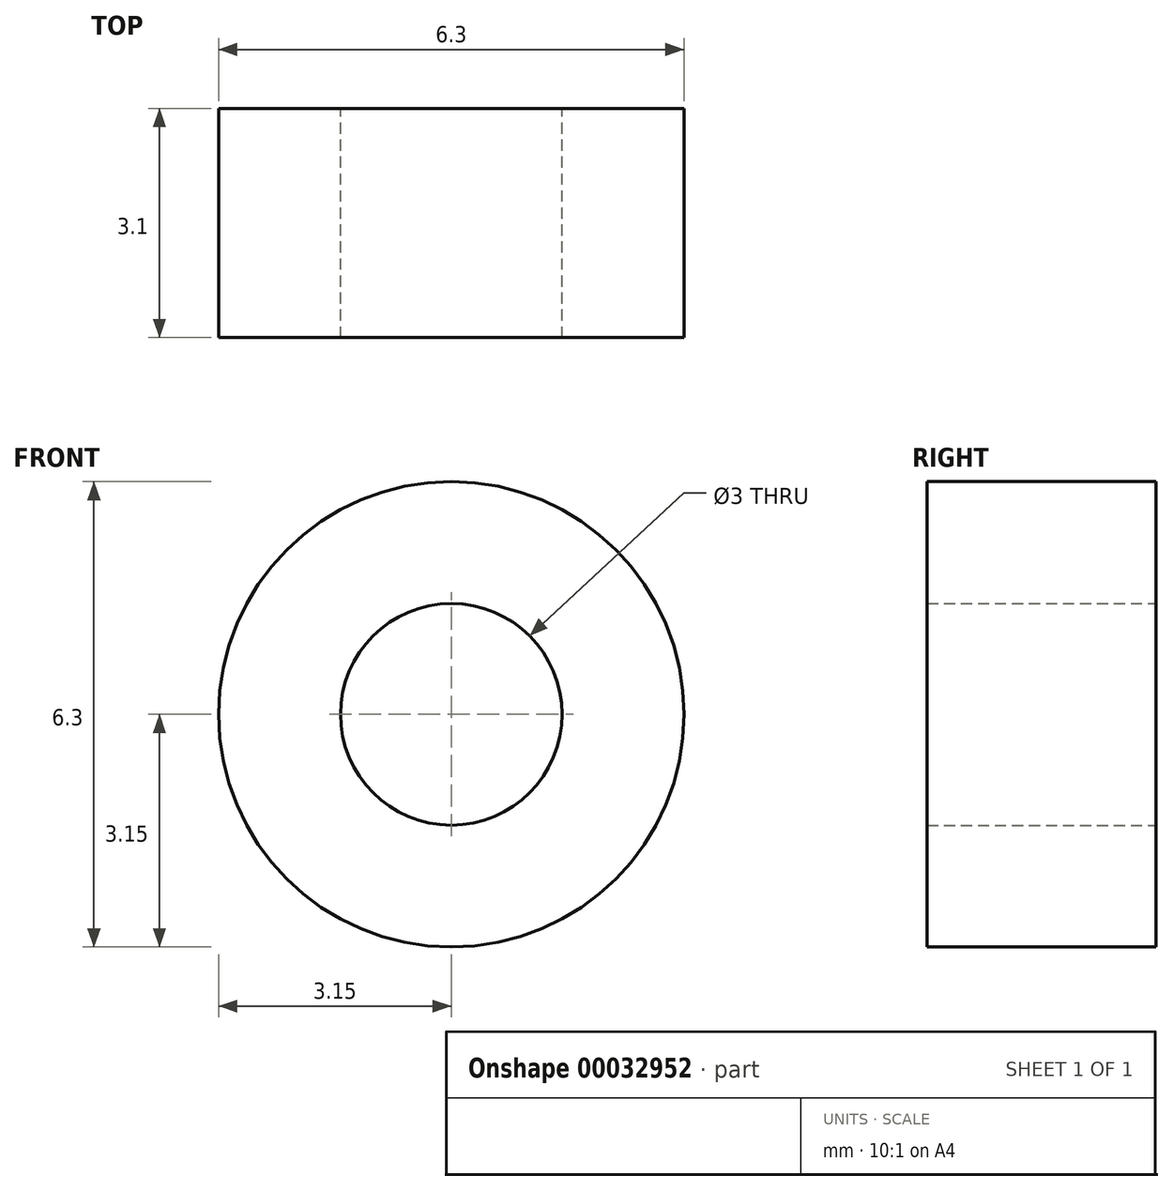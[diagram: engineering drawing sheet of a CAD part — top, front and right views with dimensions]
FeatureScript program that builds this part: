
annotation { "Feature Type Name" : "Feature", "Feature Type Description" : "" }
export const myFeature = defineFeature(function(context is Context, id is Id, definition is map)
    precondition{}
    {
        {
            var Q0;
            Q0=qCreatedBy(makeId("Front.planeOp"),FACE);
            var sketch = newSketch(context, id + "F0", { "sketchPlane" : qUnion([Q0])});
            skCircle(sketch, "E0", {"center": v(0, 0) * mm, "radius": 1.5 * mm});
            skCircle(sketch, "E1", {"center": v(0, 0) * mm, "radius": 3.15 * mm});
            skSolve(sketch);
        }
        {
            var Q0;
            Q0=qSketchRegion(id+"F0",true);
            extrude(context, id + "F1", {"entities" : qUnion([Q0]), "depth" : 3.1 * mm});
        }
    });
